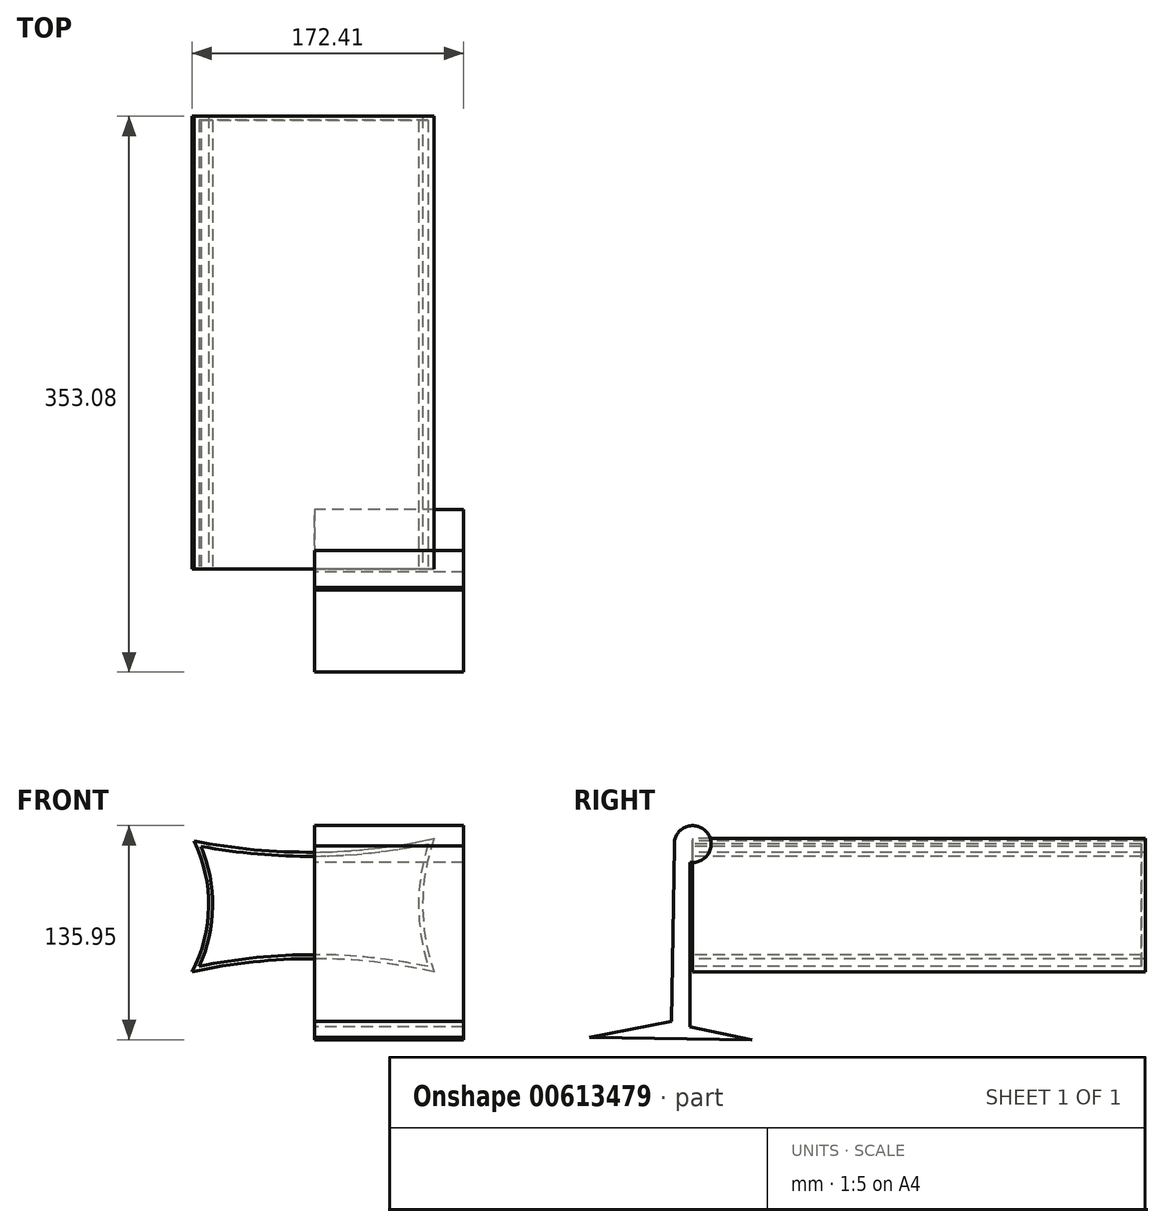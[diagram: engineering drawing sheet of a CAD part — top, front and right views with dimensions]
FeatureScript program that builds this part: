
annotation { "Feature Type Name" : "Feature", "Feature Type Description" : "" }
export const myFeature = defineFeature(function(context is Context, id is Id, definition is map)
    precondition{}
    {
        {
            var Q0;
            Q0=qCreatedBy(makeId("Front.planeOp"),FACE);
            var sketch = newSketch(context, id + "F0", { "sketchPlane" : qUnion([Q0])});
            skArc(sketch, "E0", {"start": v(-76.3, 50.21) * mm, "mid": v(-0.02, 43.08) * mm, "end": v(76.1, 51.78) * mm});
            skArc(sketch, "E1", {"start": v(76.1, 51.78) * mm, "mid": v(68.78, 9.38) * mm, "end": v(76.1, -33.02) * mm});
            skArc(sketch, "E2", {"start": v(76.1, -33.02) * mm, "mid": v(-0.78, -24.55) * mm, "end": v(-77.67, -33.02) * mm});
            skArc(sketch, "E3", {"start": v(-77.67, -33.02) * mm, "mid": v(-67.14, 8.44) * mm, "end": v(-76.3, 50.21) * mm});
            skSolve(sketch);
        }
        {
            var Q0;
            Q0 = qSketchRegion(id + "F0", true);
            extrude(context, id + "F1", {"entities" : qUnion([Q0]), "oppositeDirection" : true, "depth" : 287.53 * mm, "offsetDistance" : 25.4 * mm});
        }
        {
            var Q0;
            Q0=makeQuery(id+"F1.opExtrude","CAP_FACE",FACE,{"disambiguationData":[OSD([sQuery(id+"F0.wireOp",EDGE,"E0"),sQuery(id+"F0.wireOp",EDGE,"E1"),sQuery(id+"F0.wireOp",EDGE,"E2"),sQuery(id+"F0.wireOp",EDGE,"E3")])],"isStart":true});
            shell(context, id + "F2", {"entities" : qUnion([Q0]), "thickness" : 2.54 * mm});
        }
        {
            var Q0;
            Q0=qCreatedBy(makeId("Right.planeOp"),FACE);
            var sketch = newSketch(context, id + "F3", { "sketchPlane" : qUnion([Q0])});
            skArc(sketch, "E4", {"start": v(-1.86, 36.72) * mm, "mid": v(8.45, 56.34) * mm, "end": v(-11.61, 46.92) * mm});
            skLineSegment(sketch, "E5", {"start": v(-11.61, 46.92) * mm, "end": v(-13.38, -64.28) * mm});
            skLineSegment(sketch, "E6", {"start": v(-13.38, -64.28) * mm, "end": v(-65.55, -74.44) * mm});
            skLineSegment(sketch, "E7", {"start": v(-65.55, -74.44) * mm, "end": v(37.8, -76) * mm});
            skLineSegment(sketch, "E8", {"start": v(37.8, -76) * mm, "end": v(-1.86, -67.8) * mm});
            skLineSegment(sketch, "E9", {"start": v(-1.86, -67.8) * mm, "end": v(-1.86, 36.72) * mm});
            skSolve(sketch);
        }
        {
            var Q0;
            Q0 = qSketchRegion(id + "F3", true);
            extrude(context, id + "F4", {"entities" : qUnion([Q0]), "depth" : 94.74 * mm, "offsetDistance" : 25.4 * mm});
        }
    });
